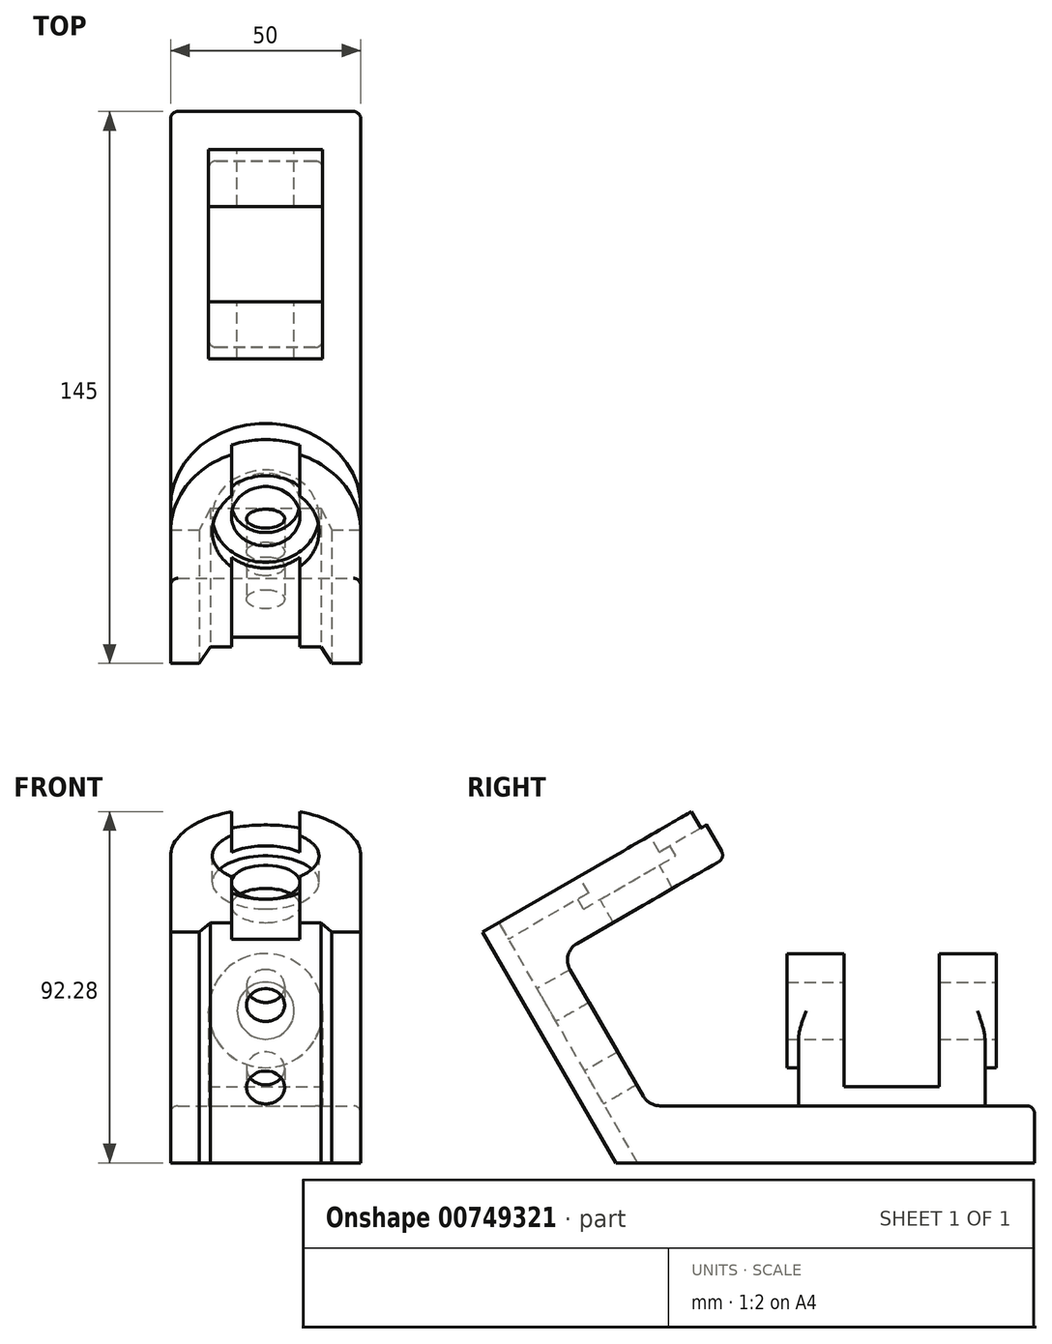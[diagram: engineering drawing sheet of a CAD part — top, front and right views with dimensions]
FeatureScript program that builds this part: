
annotation { "Feature Type Name" : "Feature", "Feature Type Description" : "" }
export const myFeature = defineFeature(function(context is Context, id is Id, definition is map)
    precondition{}
    {
        {
            var Q0;
            Q0=qCreatedBy(makeId("Right.planeOp"),FACE);
            var sketch = newSketch(context, id + "F0", { "sketchPlane" : qUnion([Q0])});
            skLineSegment(sketch, "E0", {"start": v(0, 15) * mm, "end": v(0, 0) * mm});
            skLineSegment(sketch, "E1", {"start": v(0, 0) * mm, "end": v(-110, 0) * mm});
            skLineSegment(sketch, "E2", {"start": v(-110, 0) * mm, "end": v(-145, 60.62) * mm});
            skLineSegment(sketch, "E3", {"start": v(-145, 60.62) * mm, "end": v(-88.7, 93.12) * mm});
            skLineSegment(sketch, "E4", {"start": v(-88.7, 93.12) * mm, "end": v(-81.2, 80.13) * mm});
            skLineSegment(sketch, "E5", {"start": v(-81.2, 80.13) * mm, "end": v(-124.5, 55.13) * mm});
            skLineSegment(sketch, "E6", {"start": v(0, 15) * mm, "end": v(-101.34, 15) * mm});
            skLineSegment(sketch, "E7.0", {"start": v(-101.34, 15) * mm, "end": v(-124.5, 55.13) * mm});
            skSolve(sketch);
        }
        {
            var Q0;
            Q0 = qSketchRegion(id + "F0", true);
            extrude(context, id + "F1", {"entities" : qUnion([Q0]), "oppositeDirection" : true, "depth" : 50 * mm, "offsetDistance" : 25 * mm});
        }
        {
            var Q0;
            Q0=makeQuery(id+"F1.opExtrude","CAP_EDGE",EDGE,{"disambiguationData":[OSD([sQuery(id+"F0.wireOp",EDGE,"E4")])],"isStart":true});
            var Q1;
            Q1=makeQuery(id+"F1.opExtrude","CAP_EDGE",EDGE,{"disambiguationData":[OSD([sQuery(id+"F0.wireOp",EDGE,"E4")])],"isStart":false});
            fillet(context, id + "F2", {"entities" : qUnion([Q0, Q1]), "radius" : 25 * mm, "tangentPropagation" : true, "allowEdgeOverflow" : false});
        }
        {
            var Q0;
            Q0=makeQuery(id+"F1.opExtrude","SWEPT_FACE",FACE,{"disambiguationData":[OSD([sQuery(id+"F0.wireOp",EDGE,"E0")])]});
            cPlane(context, id + "F3", {"entities" : qUnion([Q0]), "cplaneType" : CPlaneType.OFFSET, "offset" : 13 * mm, "oppositeDirection" : true, "width" : 150 * mm, "height" : 150 * mm});
        }
        {
            var Q0;
            Q0=qCreatedBy(id+"F3.planeOp",FACE);
            var sketch = newSketch(context, id + "F4", { "sketchPlane" : qUnion([Q0])});
            skLineSegment(sketch, "E8.0", {"start": v(50, 0) * mm, "end": v(0, 0) * mm, "construction": true});
            skLineSegment(sketch, "E9", {"start": v(25, 0) * mm, "end": v(25, 40) * mm, "construction": true});
            skCircle(sketch, "E10", {"center": v(25, 40) * mm, "radius": 7.5 * mm});
            skCircle(sketch, "E11", {"center": v(25, 40) * mm, "radius": 15 * mm});
            skLineSegment(sketch, "E12.0", {"start": v(40, 15) * mm, "end": v(10, 15) * mm});
            skLineSegment(sketch, "E13", {"start": v(10, 40) * mm, "end": v(10, 15) * mm});
            skLineSegment(sketch, "E14", {"start": v(40, 40) * mm, "end": v(40, 15) * mm});
            skPoint(sketch, "E15.orphan", {"position": v(0, 15) * mm});
            skPoint(sketch, "E16.orphan", {"position": v(50, 15) * mm});
            skSolve(sketch);
        }
        {
            var Q0;
            Q0=makeQuery(id+"F4.imprint","IMPRINT",FACE,{"disambiguationData":[TD([[makeQuery(id+"F4.imprint","IMPRINT",EDGE,{"derivedFrom":sQuery(id+"F4.wireOp",EDGE,"E10")}),-1.0]])]});
            extrude(context, id + "F5", {"entities" : qUnion([Q0]), "oppositeDirection" : true, "depth" : (55 - 3) * mm, "offsetDistance" : 25 * mm, "hasSecondDirection" : true, "secondDirectionOppositeDirection" : false, "secondDirectionDepth" : 3 * mm});
        }
        {
            var Q0;
            Q0=makeQuery(id+"F4.imprint","IMPRINT",FACE,{"disambiguationData":[TD([[makeQuery(id+"F4.imprint","IMPRINT",EDGE,{"derivedFrom":sQuery(id+"F4.wireOp",EDGE,"E12.0")}),-1.0]])]});
            extrude(context, id + "F6", {"entities" : qUnion([Q0]), "operationType" : NewBodyOperationType.ADD, "oppositeDirection" : true, "depth" : (55 - 3 - 3) * mm, "offsetDistance" : 25 * mm});
        }
        {
            var Q0;
            Q0=makeQuery(id+"F6.opExtrude","SWEPT_FACE",FACE,{"disambiguationData":[OSD([sQuery(id+"F4.wireOp",EDGE,"E13")])]});
            var sketch = newSketch(context, id + "F7", { "sketchPlane" : qUnion([Q0])});
            skLineSegment(sketch, "E17", {"start": v(-65, 55) * mm, "end": v(-10, 55) * mm});
            skLineSegment(sketch, "E18.bottom", {"start": v(-50, 55) * mm, "end": v(-25, 55) * mm});
            skLineSegment(sketch, "E18.top", {"start": v(-50, 20) * mm, "end": v(-25, 20) * mm});
            skLineSegment(sketch, "E18.left", {"start": v(-50, 55) * mm, "end": v(-50, 20) * mm});
            skLineSegment(sketch, "E18.right", {"start": v(-25, 55) * mm, "end": v(-25, 20) * mm});
            skLineSegment(sketch, "E19.0", {"start": v(-65, 55) * mm, "end": v(-65, 25) * mm, "construction": true});
            skLineSegment(sketch, "E20", {"start": v(-65, 40) * mm, "end": v(-13, 40) * mm, "construction": true});
            skSolve(sketch);
        }
        {
            var Q0;
            Q0 = qSketchRegion(id + "F7", true);
            extrude(context, id + "F8", {"entities" : qUnion([Q0]), "operationType" : NewBodyOperationType.REMOVE, "endBound" : BoundingType.THROUGH_ALL, "oppositeDirection" : true, "depth" : 25 * mm, "offsetDistance" : 25 * mm});
        }
        {
            var Q0;
            Q0=makeQuery(id+"F1.opExtrude","SWEPT_FACE",FACE,{"disambiguationData":[OSD([sQuery(id+"F0.wireOp",EDGE,"E3")])]});
            var sketch = newSketch(context, id + "F9", { "sketchPlane" : qUnion([Q0])});
            skLineSegment(sketch, "E21.0", {"start": v(-50, -95.26) * mm, "end": v(0, -95.26) * mm});
            skLineSegment(sketch, "E22", {"start": v(-25, -95.26) * mm, "end": v(-25, -55.26) * mm, "construction": true});
            skLineSegment(sketch, "E23.0", {"start": v(-50, -90.26) * mm, "end": v(0, -90.26) * mm});
            skLineSegment(sketch, "E24", {"start": v(-39.5, -90.26) * mm, "end": v(-42.39, -95.26) * mm});
            skLineSegment(sketch, "E25.MirrorCS", {"start": v(-10.5, -90.26) * mm, "end": v(-7.61, -95.26) * mm});
            skCircle(sketch, "E26", {"center": v(-25, -55.26) * mm, "radius": 14 * mm});
            skCircle(sketch, "E27", {"center": v(-25, -55.26) * mm, "radius": 9 * mm});
            skSolve(sketch);
        }
        {
            var Q0;
            {var subQ0=sQuery(id+"F9.wireOp",EDGE,"E24");Q0=makeQuery(id+"F9.imprint","IMPRINT",FACE,{"disambiguationData":[TD([[makeQuery(id+"F9.imprint","IMPRINT",EDGE,{"derivedFrom":subQ0}),1.0]])]});}
            extrude(context, id + "F10", {"entities" : qUnion([Q0]), "operationType" : NewBodyOperationType.REMOVE, "endBound" : BoundingType.THROUGH_ALL, "oppositeDirection" : true, "depth" : 25 * mm, "offsetDistance" : 25 * mm});
        }
        {
            var Q0;
            Q0=makeQuery(id+"F10.boolean.opBoolean","COPY",FACE,{"derivedFrom":makeQuery(id+"F10.opExtrude","SWEPT_FACE",FACE,{"disambiguationData":[OSD([sQuery(id+"F9.wireOp",EDGE,"E23.0")])]})});
            var sketch = newSketch(context, id + "F11", { "sketchPlane" : qUnion([Q0])});
            skLineSegment(sketch, "E28.0", {"start": v(-39.5, 125) * mm, "end": v(-10.5, 125) * mm, "construction": true});
            skLineSegment(sketch, "E29", {"start": v(-25, 125) * mm, "end": v(-25, 100) * mm, "construction": true});
            skLineSegment(sketch, "E30.bottom", {"start": v(-34, 125) * mm, "end": v(-16, 125) * mm});
            skLineSegment(sketch, "E30.top", {"start": v(-34, 120) * mm, "end": v(-16, 120) * mm});
            skLineSegment(sketch, "E30.left", {"start": v(-34, 125) * mm, "end": v(-34, 120) * mm});
            skLineSegment(sketch, "E30.right", {"start": v(-16, 125) * mm, "end": v(-16, 120) * mm});
            skPoint(sketch, "E31", {"position": v(-25, 100) * mm});
            skPoint(sketch, "E32", {"position": v(-25, 75) * mm});
            skSolve(sketch);
        }
        {
            var Q0;
            Q0 = qSketchRegion(id + "F11", true);
            extrude(context, id + "F12", {"entities" : qUnion([Q0]), "operationType" : NewBodyOperationType.REMOVE, "endBound" : BoundingType.THROUGH_ALL, "oppositeDirection" : true, "depth" : 25 * mm, "offsetDistance" : 25 * mm});
        }
        {
            var Q0;
            Q0=sQuery(id+"F11.wireOp",VERTEX,"E31");
            var Q1;
            Q1=sQuery(id+"F11.wireOp",VERTEX,"E32");
            var Q2;
            Q2=makeQuery(id+"F1.opExtrude","SWEPT_BODY",BODY,{"disambiguationData":[OSD([sQuery(id+"F0.wireOp",EDGE,"E0"),sQuery(id+"F0.wireOp",EDGE,"E1"),sQuery(id+"F0.wireOp",EDGE,"E2"),sQuery(id+"F0.wireOp",EDGE,"E3"),sQuery(id+"F0.wireOp",EDGE,"E4"),sQuery(id+"F0.wireOp",EDGE,"E5"),sQuery(id+"F0.wireOp",EDGE,"E6"),sQuery(id+"F0.wireOp",EDGE,"E7.0")])]});
            hole(context, id + "F13", {"style" : HoleStyle.SIMPLE, "endStyle" : HoleEndStyle.BLIND, "holeDiameter" : 10 * mm, "majorDiameter" : 5 * mm, "holeDepth" : 10 * mm, "tappedDepth" : 12 * mm, "tapClearance" : 3, "startFromSketch" : true, "locations" : qUnion([Q0, Q1]), "scope" : qUnion([Q2])});
        }
        {
            var Q0;
            Q0=makeQuery(id+"F9.imprint","IMPRINT",FACE,{"disambiguationData":[TD([[makeQuery(id+"F9.imprint","IMPRINT",EDGE,{"derivedFrom":sQuery(id+"F9.wireOp",EDGE,"E26")}),1.0]])]});
            var Q1;
            Q1=makeQuery(id+"F9.imprint","IMPRINT",FACE,{"disambiguationData":[TD([[makeQuery(id+"F9.imprint","IMPRINT",EDGE,{"derivedFrom":sQuery(id+"F9.wireOp",EDGE,"E27")}),1.0]])]});
            extrude(context, id + "F14", {"entities" : qUnion([Q0, Q1]), "operationType" : NewBodyOperationType.REMOVE, "oppositeDirection" : true, "depth" : 8 * mm, "offsetDistance" : 25 * mm});
        }
        {
            var Q0;
            Q0=makeQuery(id+"F9.imprint","IMPRINT",FACE,{"disambiguationData":[TD([[makeQuery(id+"F9.imprint","IMPRINT",EDGE,{"derivedFrom":sQuery(id+"F9.wireOp",EDGE,"E27")}),1.0]])]});
            extrude(context, id + "F15", {"entities" : qUnion([Q0]), "operationType" : NewBodyOperationType.REMOVE, "oppositeDirection" : true, "depth" : 15 * mm, "offsetDistance" : 25 * mm});
        }
        {
            var Q0;
            Q0=makeQuery(id+"F1.opExtrude","SWEPT_EDGE",EDGE,{"disambiguationData":[OSD([sQuery(id+"F0.wireOp",EDGE,"E5"),sQuery(id+"F0.wireOp",EDGE,"E7.0")])]});
            var Q1;
            Q1=makeQuery(id+"F1.opExtrude","SWEPT_EDGE",EDGE,{"disambiguationData":[OSD([sQuery(id+"F0.wireOp",EDGE,"E6"),sQuery(id+"F0.wireOp",EDGE,"E7.0")])]});
            fillet(context, id + "F16", {"entities" : qUnion([Q0, Q1]), "radius" : 5 * mm, "tangentPropagation" : true, "allowEdgeOverflow" : false});
        }
        {
            var Q0;
            Q0=makeQuery(id+"F1.opExtrude","CAP_EDGE",EDGE,{"disambiguationData":[OSD([sQuery(id+"F0.wireOp",EDGE,"E0")])],"isStart":true});
            var Q1;
            Q1=makeQuery(id+"F1.opExtrude","CAP_EDGE",EDGE,{"disambiguationData":[OSD([sQuery(id+"F0.wireOp",EDGE,"E0")])],"isStart":false});
            var Q2;
            Q2=makeQuery(id+"F1.opExtrude","CAP_EDGE",EDGE,{"disambiguationData":[OSD([sQuery(id+"F0.wireOp",EDGE,"E6")])],"isStart":true});
            var Q3;
            Q3=makeQuery(id+"F1.opExtrude","SWEPT_EDGE",EDGE,{"disambiguationData":[OSD([sQuery(id+"F0.wireOp",EDGE,"E0"),sQuery(id+"F0.wireOp",EDGE,"E6")])]});
            var Q4;
            Q4=makeQuery(id+"F6.opExtrude","CAP_EDGE",EDGE,{"disambiguationData":[OSD([sQuery(id+"F4.wireOp",EDGE,"E13")])],"isStart":false});
            var Q5;
            Q5=makeQuery(id+"F6.opExtrude","CAP_EDGE",EDGE,{"disambiguationData":[OSD([sQuery(id+"F4.wireOp",EDGE,"E13")])],"isStart":true});
            var Q6;
            Q6=makeQuery(id+"F6.opExtrude","CAP_EDGE",EDGE,{"disambiguationData":[OSD([sQuery(id+"F4.wireOp",EDGE,"E14")])],"isStart":true});
            var Q7;
            Q7=makeQuery(id+"F6.opExtrude","CAP_EDGE",EDGE,{"disambiguationData":[OSD([sQuery(id+"F4.wireOp",EDGE,"E14")])],"isStart":false});
            var Q8;
            Q8=makeQuery(id+"F6.opExtrude","SWEPT_EDGE",EDGE,{"disambiguationData":[OSD([sQuery(id+"F4.wireOp",EDGE,"E12.0"),sQuery(id+"F4.wireOp",EDGE,"E14")])]});
            var Q9;
            Q9=makeQuery(id+"F6.opExtrude","CAP_EDGE",EDGE,{"disambiguationData":[OSD([sQuery(id+"F4.wireOp",EDGE,"E11")])],"isStart":false});
            var Q10;
            Q10=makeQuery(id+"F6.opExtrude","CAP_EDGE",EDGE,{"disambiguationData":[OSD([sQuery(id+"F4.wireOp",EDGE,"E11")])],"isStart":true});
            fillet(context, id + "F17", {"entities" : qUnion([Q0, Q1, Q2, Q3, Q4, Q5, Q6, Q7, Q8, Q9, Q10]), "radius" : 2 * mm, "tangentPropagation" : true, "allowEdgeOverflow" : false});
        }
    });
